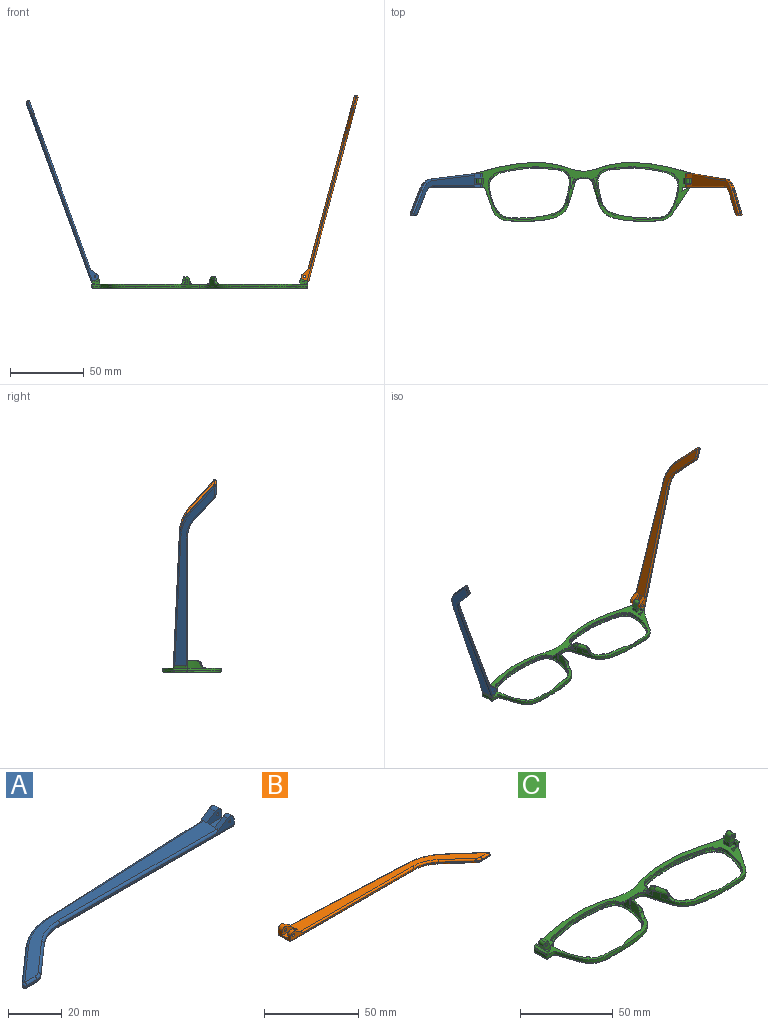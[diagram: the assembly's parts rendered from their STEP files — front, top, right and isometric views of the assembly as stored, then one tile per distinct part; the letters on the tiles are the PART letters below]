
ASSEMBLY  parts=3 mates=2
PART A: 43 faces, bbox 130.2x29.5x5.9 mm
  f0: plane 9.62x3.72mm, normal (1,0,0), area 24.7mm2, adj f1,f3,f4,f5,f10,f16,f18,f28
  f1: cylinder r=2.2mm len=3.45mm, axis (0,-1,0), area 11mm2, adj f0,f2,f4,f37
  f2: plane 6.01x3.91mm, normal (-0.55,0,0.84), area 12.7mm2, adj f1,f4,f9,f19,f37
  f3: plane 2.26x0.1mm, normal (0,0,1), area 0.1mm2, adj f0,f5,f18
  f4: plane 92.1x4.9mm, normal (0,-1,0), area 79.9mm2, adj f0,f1,f2,f14,f19,f36,f42
  f5: plane 93.42x4.13mm, normal (-0.04,1,0), area 64.8mm2, adj f0,f3,f11,f15,f17,f27,f28
  f6: plane 17.82x15.72mm, normal (-0.66,0.75,0), area 14.3mm2, adj f11,f12,f25,f30
  f7: plane 5.46x0.6mm, normal (0,-1,0), area 3.3mm2, adj f12,f13,f23,f32
  f8: plane 14.99x13.23mm, normal (0.66,-0.75,0), area 12mm2, adj f13,f14,f21,f34
  f9: plane 121.18x26.73mm, normal (0,0,1), area 627.7mm2, adj f2,f17,f19,f20,f21,f22,f23,f25
  f10: plane 129.1x27.08mm, normal (0,0,-1), area 686.5mm2, adj f0,f28,f29,f30,f32,f33,f34,f35
  f11: cylinder r=30mm len=18.52mm, axis (0,0,-1), area 12.2mm2, adj f5,f6,f26,f29
  f12: cylinder r=1mm len=1.75mm, axis (0,0,-1), area 1.5mm2, adj f6,f7,f24,f31
  f13: cylinder r=5mm len=3.31mm, axis (0,0,-1), area 2.2mm2, adj f7,f8,f22,f33
  f14: cylinder r=20mm len=13.23mm, axis (0,0,1), area 8.7mm2, adj f4,f8,f20,f35
  f15: plane 5.66x0.25mm, normal (0,0,-1), area 0.7mm2, adj f5,f17,f18
  f16: cylinder r=2.2mm len=3.45mm, axis (0,-1,0), area 14.8mm2, adj f0,f17,f18,f38
  f17: plane 6.01x3.91mm, normal (-0.55,0,0.84), area 16.9mm2, adj f5,f9,f15,f16,f18,f27,f38
  f18: plane 7.92x3.3mm, normal (0,1,0), area 15.9mm2, adj f0,f3,f15,f16,f17,f41
  f19: cylinder r=1mm len=84.18mm, axis (-1,0,0), area 131.4mm2, adj f2,f4,f9,f20
  f20: torus R=21mm, axis (0,0,1), area 23.1mm2, adj f9,f14,f19,f21
  f21: cylinder r=1mm len=15.65mm, axis (-0.75,-0.66,0), area 31.4mm2, adj f8,f9,f20,f22
  f22: torus R=4mm, axis (0,0,1), area 5.3mm2, adj f9,f13,f21,f23
  f23: cylinder r=1mm len=5.46mm, axis (-1,0,0), area 8.6mm2, adj f7,f9,f22,f24
  f24: sphere r=1mm, area 2.4mm2, adj f12,f23,f25
  f25: cylinder r=1mm len=18.48mm, axis (0.75,0.66,0), area 37.3mm2, adj f6,f9,f24,f26
  f26: torus R=29mm, axis (0,0,1), area 31.6mm2, adj f9,f11,f25,f27
  f27: cylinder r=1mm len=85.5mm, axis (1,0.04,0), area 133.5mm2, adj f5,f9,f17,f26
  f28: cylinder r=1mm len=93.46mm, axis (-1,-0.04,0), area 146.9mm2, adj f0,f5,f10,f29
  f29: torus R=29mm, axis (0,0,1), area 31.6mm2, adj f10,f11,f28,f30
  f30: cylinder r=1mm len=18.48mm, axis (-0.75,-0.66,0), area 37.3mm2, adj f6,f10,f29,f31
  f31: sphere r=1mm, area 2.4mm2, adj f12,f30,f32
  f32: cylinder r=1mm len=5.46mm, axis (1,0,0), area 8.6mm2, adj f7,f10,f31,f33
  f33: torus R=4mm, axis (0,0,1), area 5.3mm2, adj f10,f13,f32,f34
  f34: cylinder r=1mm len=15.65mm, axis (0.75,0.66,0), area 31.4mm2, adj f8,f10,f33,f35
  f35: torus R=21mm, axis (0,0,1), area 23.1mm2, adj f10,f14,f34,f36
  f36: cylinder r=1mm len=92.1mm, axis (1,0,0), area 144.7mm2, adj f0,f4,f10,f35
  f37: plane 7.92x4.7mm, normal (0,1,0), area 27mm2, adj f0,f1,f2,f39,f40,f42
  f38: plane 7.92x4.7mm, normal (0,-1,0), area 27mm2, adj f0,f16,f17,f39,f40,f41
  f39: plane 7.92x4.1mm, normal (0,0,1), area 32.5mm2, adj f0,f37,f38,f40
  f40: plane 4.1x1.4mm, normal (1,0,0), area 5.7mm2, adj f9,f37,f38,f39
  f41: cylinder r=0.5mm len=3.1mm, axis (0,-1,0), area 9.7mm2, adj f18,f38
  f42: cylinder r=0.5mm len=2.3mm, axis (0,-1,0), area 7.2mm2, adj f4,f37
PART B: 43 faces, bbox 130.2x29.5x5.9 mm
  f0: plane 9.62x3.72mm, normal (-1,0,0), area 24.7mm2, adj f1,f3,f4,f5,f10,f16,f18,f28
  f1: cylinder r=2.2mm len=3.45mm, axis (0,-1,0), area 11mm2, adj f0,f2,f4,f37
  f2: plane 6.01x3.91mm, normal (0.55,0,0.84), area 12.7mm2, adj f1,f4,f9,f19,f37
  f3: plane 2.26x0.1mm, normal (0,0,1), area 0.1mm2, adj f0,f5,f18
  f4: plane 92.1x4.9mm, normal (0,-1,0), area 78.2mm2, adj f0,f1,f2,f14,f19,f36,f42
  f5: plane 93.42x4.13mm, normal (0.04,1,0), area 64.8mm2, adj f0,f3,f11,f15,f17,f27,f28
  f6: plane 17.82x15.72mm, normal (0.66,0.75,0), area 14.3mm2, adj f11,f12,f25,f30
  f7: plane 5.46x0.6mm, normal (0,-1,0), area 3.3mm2, adj f12,f13,f23,f32
  f8: plane 14.99x13.23mm, normal (-0.66,-0.75,0), area 12mm2, adj f13,f14,f21,f34
  f9: plane 121.18x26.73mm, normal (0,0,1), area 627.7mm2, adj f2,f17,f19,f20,f21,f22,f23,f25
  f10: plane 129.1x27.08mm, normal (0,0,-1), area 686.5mm2, adj f0,f28,f29,f30,f32,f33,f34,f35
  f11: cylinder r=30mm len=18.52mm, axis (0,0,-1), area 12.2mm2, adj f5,f6,f26,f29
  f12: cylinder r=1mm len=1.75mm, axis (0,0,-1), area 1.5mm2, adj f6,f7,f24,f31
  f13: cylinder r=5mm len=3.31mm, axis (0,0,-1), area 2.2mm2, adj f7,f8,f22,f33
  f14: cylinder r=20mm len=13.23mm, axis (0,0,1), area 8.7mm2, adj f4,f8,f20,f35
  f15: plane 5.66x0.25mm, normal (0,0,-1), area 0.7mm2, adj f5,f17,f18
  f16: cylinder r=2.2mm len=3.45mm, axis (0,-1,0), area 14.8mm2, adj f0,f17,f18,f38
  f17: plane 6.01x3.91mm, normal (0.55,0,0.84), area 16.9mm2, adj f5,f9,f15,f16,f18,f27,f38
  f18: plane 7.92x3.3mm, normal (0,1,0), area 14.3mm2, adj f0,f3,f15,f16,f17,f41
  f19: cylinder r=1mm len=84.18mm, axis (1,0,0), area 131.4mm2, adj f2,f4,f9,f20
  f20: torus R=21mm, axis (0,0,1), area 23.1mm2, adj f9,f14,f19,f21
  f21: cylinder r=1mm len=15.65mm, axis (0.75,-0.66,0), area 31.4mm2, adj f8,f9,f20,f22
  f22: torus R=4mm, axis (0,0,1), area 5.3mm2, adj f9,f13,f21,f23
  f23: cylinder r=1mm len=5.46mm, axis (1,0,0), area 8.6mm2, adj f7,f9,f22,f24
  f24: sphere r=1mm, area 2.4mm2, adj f12,f23,f25
  f25: cylinder r=1mm len=18.48mm, axis (-0.75,0.66,0), area 37.3mm2, adj f6,f9,f24,f26
  f26: torus R=29mm, axis (0,0,1), area 31.6mm2, adj f9,f11,f25,f27
  f27: cylinder r=1mm len=85.5mm, axis (-1,0.04,0), area 133.5mm2, adj f5,f9,f17,f26
  f28: cylinder r=1mm len=93.46mm, axis (1,-0.04,0), area 146.9mm2, adj f0,f5,f10,f29
  f29: torus R=29mm, axis (0,0,1), area 31.6mm2, adj f10,f11,f28,f30
  f30: cylinder r=1mm len=18.48mm, axis (0.75,-0.66,0), area 37.3mm2, adj f6,f10,f29,f31
  f31: sphere r=1mm, area 2.4mm2, adj f12,f30,f32
  f32: cylinder r=1mm len=5.46mm, axis (-1,0,0), area 8.6mm2, adj f7,f10,f31,f33
  f33: torus R=4mm, axis (0,0,1), area 5.3mm2, adj f10,f13,f32,f34
  f34: cylinder r=1mm len=15.65mm, axis (-0.75,0.66,0), area 31.4mm2, adj f8,f10,f33,f35
  f35: torus R=21mm, axis (0,0,1), area 23.1mm2, adj f10,f14,f34,f36
  f36: cylinder r=1mm len=92.1mm, axis (-1,0,0), area 144.7mm2, adj f0,f4,f10,f35
  f37: plane 7.92x4.7mm, normal (0,1,0), area 25.4mm2, adj f0,f1,f2,f39,f40,f42
  f38: plane 7.92x4.7mm, normal (0,-1,0), area 25.4mm2, adj f0,f16,f17,f39,f40,f41
  f39: plane 7.92x4.1mm, normal (0,0,1), area 32.5mm2, adj f0,f37,f38,f40
  f40: plane 4.1x1.4mm, normal (-1,0,0), area 5.7mm2, adj f9,f37,f38,f39
  f41: cylinder r=0.88mm len=3.1mm, axis (0,-1,0), area 17mm2, adj f18,f38
  f42: cylinder r=0.88mm len=2.3mm, axis (0,-1,0), area 12.6mm2, adj f4,f37
PART C: 120 faces, bbox 148.1x40.9x17.9 mm
  f0: bspline ~1.82x1.22mm, area 0.7mm2, adj f2,f7,f38,f53
  f1: plane 147.57x40.34mm, normal (0,0,1), area 849mm2, adj f4,f5,f6,f7,f8,f9,f13,f21
  f2: bspline ~6.1x4.93mm, area 12.7mm2, adj f0,f7,f38,f42,f44,f53,f54
  f3: plane 4.46x1.45mm, normal (0,0,1), area 0.1mm2, adj f7,f39
  f4: plane 1.23x0.04mm, normal (0,0,1), area 0mm2, adj f1,f7,f23
  f5: plane 6.97x5.07mm, normal (0,1,0), area 22.7mm2, adj f1,f21,f22,f26,f28,f29,f31,f32
  f6: plane 3.2x2.36mm, normal (0,-1,0), area 5.7mm2, adj f1,f21,f27,f30
  f7: extruded ~73.26x39.84mm, area 292.7mm2, adj f0,f1,f2,f3,f4,f8,f14,f15
  f8: extruded ~35.39x5.69mm, area 72.2mm2, adj f1,f7,f19,f68
  f9: extruded ~9.91x2mm, area 20.1mm2, adj f1,f12,f13,f20
  f10: plane 144.78x37.85mm, normal (0,0,-1), area 582.4mm2, adj f14,f16,f18,f19,f20,f73,f75,f77
  f11: plane 56.11x36.01mm, normal (0,0,1), area 126.3mm2, adj f12,f20
  f12: extruded ~55.66x35.79mm, area 147mm2, adj f9,f11,f13
  f13: extruded ~55.66x35.79mm, area 197.8mm2, adj f1,f9,f12,f40,f41,f42,f43,f44
  f14: bspline ~73.27x30.39mm, area 161.7mm2, adj f7,f10,f15,f73
  f15: bspline ~1x1mm, area 0.8mm2, adj f7,f14,f16
  f16: bspline ~8.99x1.23mm, area 12.6mm2, adj f7,f10,f15,f17
  f17: bspline ~1.04x1mm, area 0.7mm2, adj f7,f16,f18
  f18: bspline ~45.86x8.59mm, area 59.8mm2, adj f7,f10,f17,f19
  f19: bspline ~37.01x6.7mm, area 56.6mm2, adj f8,f10,f18,f78
  f20: bspline ~56.23x35.9mm, area 235.3mm2, adj f9,f10,f11
  f21: plane 4x2.36mm, normal (-1,0,0), area 9.5mm2, adj f1,f5,f6,f22
  f22: plane 4x0.02mm, normal (0.34,0,0.94), area 0.1mm2, adj f5,f21,f29
  f23: plane 2.76x2.53mm, normal (0,-1,0), area 3.9mm2, adj f4,f27,f28,f36,f57
  f24: plane 7.67x1.6mm, normal (0.94,0,-0.34), area 13mm2, adj f1,f36,f37,f57
  f25: plane 2.1x1.69mm, normal (0,1,0), area 2.8mm2, adj f1,f26,f28,f37,f57
  f26: plane 3.3x2.1mm, normal (-1,0,0), area 6.9mm2, adj f1,f5,f25,f28
  f27: plane 2.35x2.1mm, normal (-1,0,0), area 4.9mm2, adj f1,f6,f23,f28,f30
  f28: plane 9.65x1.24mm, normal (0,0,1), area 8.2mm2, adj f5,f23,f25,f26,f27,f30,f31,f57
  f29: plane 4x3.31mm, normal (-0.94,0,0.34), area 14.1mm2, adj f5,f22,f30,f33
  f30: plane 5.77x5.06mm, normal (0,-1,0), area 17mm2, adj f6,f27,f28,f29,f31,f32,f33,f34
  f31: plane 4x2.21mm, normal (0.94,0,-0.34), area 9.4mm2, adj f5,f28,f30,f34
  f32: plane 4x0.01mm, normal (0.34,0,0.94), area 0mm2, adj f5,f30,f33,f34
  f33: cylinder r=1.98mm len=4mm, axis (0,1,0), area 12.4mm2, adj f5,f29,f30,f32
  f34: cylinder r=1.98mm len=4mm, axis (0,-1,0), area 12.4mm2, adj f5,f30,f31,f32
  f35: cylinder r=0.88mm len=4mm, axis (0,-1,0), area 22mm2, adj f5,f30
  f36: cone r=1mm half-angle=20deg, axis (0,0,1), area 2.3mm2, adj f1,f23,f24,f57
  f37: cylinder r=1mm len=2.28mm, axis (-0.34,0,-0.94), area 3mm2, adj f1,f24,f25,f57
  f38: extruded ~3.67x3.11mm, area 5.9mm2, adj f0,f2,f7,f60
  f39: extruded ~4.44x3.32mm, area 15.1mm2, adj f3,f7,f43,f44,f56
  f40: extruded ~4.98x1.36mm, area 6.6mm2, adj f13,f42
  f41: plane 3.63x0.97mm, normal (0,0,1), area 0.3mm2, adj f13,f42,f44
  f42: bspline ~15.5x15.35mm, area 6.4mm2, adj f2,f13,f40,f41,f55
  f43: bspline ~7.26x7.26mm, area 6.3mm2, adj f13,f39,f44,f56
  f44: bspline ~10.29x4.84mm, area 21.4mm2, adj f2,f7,f13,f39,f41,f43
  f45: plane 3.19x1.37mm, normal (0,0,-1), area 2.1mm2, adj f13,f46
  f46: cylinder r=2.28mm len=3.17mm, axis (0,0,1), area 2.1mm2, adj f1,f13,f45,f55
  f47: plane 3.14x2.79mm, normal (0,0,-1), area 3.9mm2, adj f13,f48
  f48: cylinder r=2.28mm len=3.13mm, axis (0,0,1), area 2.5mm2, adj f1,f13,f47
  f49: plane 1.8x1.27mm, normal (0,0,-1), area 0.9mm2, adj f13,f50
  f50: cylinder r=1.3mm len=1.79mm, axis (0,0,1), area 1.3mm2, adj f1,f13,f49
  f51: plane 1.95x1.68mm, normal (0,0,-1), area 1.5mm2, adj f13,f52
  f52: cylinder r=1.3mm len=1.93mm, axis (0,0,1), area 1.5mm2, adj f1,f13,f51
  f53: bspline ~2.66x2.04mm, area 1.9mm2, adj f0,f2,f7,f54,f59
  f54: bspline ~3.55x3.47mm, area 3.7mm2, adj f1,f2,f53,f55,f59
  f55: bspline ~5.1x3.97mm, area 7.9mm2, adj f1,f13,f42,f46,f54
  f56: bspline ~3.7x3.66mm, area 7.8mm2, adj f1,f7,f13,f39,f43
  f57: plane 9.71x1.44mm, normal (0.34,0,0.94), area 13.9mm2, adj f23,f24,f25,f28,f36,f37
  f58: bspline ~6.38x2.14mm, area 2.6mm2, adj f1,f7,f59,f117
  f59: bspline ~2.1x1.46mm, area 0.6mm2, adj f7,f53,f54,f58
  f60: bspline ~5.24x1.75mm, area 0mm2, adj f7,f38
  f61: bspline ~2.19x1.4mm, area 0.7mm2, adj f62,f67,f97,f112
  f62: bspline ~6.1x4.93mm, area 12.6mm2, adj f61,f67,f97,f101,f103,f112,f113
  f63: plane 4.46x1.45mm, normal (0,0,1), area 0.1mm2, adj f67,f98
  f64: plane 1.23x0.04mm, normal (0,0,1), area 0mm2, adj f1,f67,f82
  f65: plane 6.97x5.07mm, normal (0,1,0), area 22.7mm2, adj f1,f80,f81,f85,f87,f88,f90,f91
  f66: plane 3.2x2.36mm, normal (0,-1,0), area 5.7mm2, adj f1,f80,f86,f89
  f67: extruded ~73.26x39.84mm, area 292.7mm2, adj f1,f7,f61,f62,f63,f64,f68,f73
  f68: extruded ~35.39x5.69mm, area 72.2mm2, adj f1,f8,f67,f78
  f69: extruded ~9.91x2mm, area 20.1mm2, adj f1,f71,f72,f79
  f70: plane 56.11x36.01mm, normal (0,0,1), area 126.3mm2, adj f71,f79
  f71: extruded ~55.66x35.79mm, area 147mm2, adj f69,f70,f72
  f72: extruded ~55.66x35.79mm, area 197.8mm2, adj f1,f69,f71,f99,f100,f101,f102,f103
  f73: bspline ~73.83x30.39mm, area 161.7mm2, adj f10,f14,f67,f74
  f74: bspline ~1x1mm, area 0.8mm2, adj f67,f73,f75
  f75: bspline ~8.99x1.23mm, area 12.6mm2, adj f10,f67,f74,f76
  f76: bspline ~1.04x1mm, area 0.8mm2, adj f67,f75,f77
  f77: bspline ~45.86x8.59mm, area 59.8mm2, adj f10,f67,f76,f78
  f78: bspline ~37.01x6.7mm, area 56.6mm2, adj f10,f19,f68,f77
  f79: bspline ~56.22x35.9mm, area 235.3mm2, adj f10,f69,f70
  f80: plane 4x2.36mm, normal (1,0,0), area 9.5mm2, adj f1,f65,f66,f81
  f81: plane 4x0.02mm, normal (-0.34,0,0.94), area 0.1mm2, adj f65,f80,f88
  f82: plane 2.76x2.53mm, normal (0,-1,0), area 3.9mm2, adj f64,f86,f87,f95,f116
  f83: plane 7.67x1.6mm, normal (-0.94,0,-0.34), area 13mm2, adj f1,f95,f96,f116
  f84: plane 2.1x1.69mm, normal (0,1,0), area 2.8mm2, adj f1,f85,f87,f96,f116
  f85: plane 3.3x2.1mm, normal (1,0,0), area 6.9mm2, adj f1,f65,f84,f87
  f86: plane 2.35x2.1mm, normal (1,0,0), area 4.9mm2, adj f1,f66,f82,f87,f89
  f87: plane 9.65x1.24mm, normal (0,0,1), area 8.2mm2, adj f65,f82,f84,f85,f86,f89,f90,f116
  f88: plane 4x3.31mm, normal (0.94,0,0.34), area 14.1mm2, adj f65,f81,f89,f92
  f89: plane 5.77x5.06mm, normal (0,-1,0), area 17mm2, adj f66,f86,f87,f88,f90,f91,f92,f93
  f90: plane 4x2.21mm, normal (-0.94,0,-0.34), area 9.4mm2, adj f65,f87,f89,f93
  f91: plane 4x0.01mm, normal (-0.34,0,0.94), area 0mm2, adj f65,f89,f92,f93
  f92: cylinder r=1.98mm len=4mm, axis (0,1,0), area 12.4mm2, adj f65,f88,f89,f91
  f93: cylinder r=1.98mm len=4mm, axis (0,-1,0), area 12.4mm2, adj f65,f89,f90,f91
  f94: cylinder r=0.88mm len=4mm, axis (0,-1,0), area 22mm2, adj f65,f89
  f95: cone r=1mm half-angle=20deg, axis (0,0,1), area 2.3mm2, adj f1,f82,f83,f116
  f96: cylinder r=1mm len=2.28mm, axis (0.34,0,-0.94), area 3mm2, adj f1,f83,f84,f116
  f97: extruded ~3.67x3.11mm, area 5.9mm2, adj f61,f62,f67,f119
  f98: extruded ~4.44x3.32mm, area 15.1mm2, adj f63,f67,f102,f103,f115
  f99: extruded ~4.98x1.36mm, area 6.6mm2, adj f72,f101
  f100: plane 3.63x0.97mm, normal (0,0,1), area 0.3mm2, adj f72,f101,f103
  f101: bspline ~15.5x15.35mm, area 6.4mm2, adj f62,f72,f99,f100,f114
  f102: bspline ~7.26x7.26mm, area 6.2mm2, adj f72,f98,f103,f115
  f103: bspline ~10.29x4.84mm, area 21.5mm2, adj f62,f67,f72,f98,f100,f102
  f104: plane 3.19x1.37mm, normal (0,0,-1), area 2.1mm2, adj f72,f105
  f105: cylinder r=2.28mm len=3.17mm, axis (0,0,1), area 2.1mm2, adj f1,f72,f104,f114
  f106: plane 3.14x2.79mm, normal (0,0,-1), area 3.9mm2, adj f72,f107
  f107: cylinder r=2.28mm len=3.13mm, axis (0,0,1), area 2.5mm2, adj f1,f72,f106
  f108: plane 1.8x1.27mm, normal (0,0,-1), area 0.9mm2, adj f72,f109
  f109: cylinder r=1.3mm len=1.79mm, axis (0,0,1), area 1.3mm2, adj f1,f72,f108
  f110: plane 1.95x1.68mm, normal (0,0,-1), area 1.5mm2, adj f72,f111
  f111: cylinder r=1.3mm len=1.93mm, axis (0,0,1), area 1.5mm2, adj f1,f72,f110
  f112: bspline ~2.65x2.03mm, area 1.9mm2, adj f61,f62,f67,f113,f118
  f113: bspline ~3.55x3.47mm, area 3.7mm2, adj f1,f62,f112,f114,f118
  f114: bspline ~5.94x4.42mm, area 7.9mm2, adj f1,f72,f101,f105,f113
  f115: bspline ~3.7x3.66mm, area 7.8mm2, adj f1,f67,f72,f98,f102
  f116: plane 9.71x1.44mm, normal (-0.34,0,0.94), area 13.9mm2, adj f82,f83,f84,f87,f95,f96
  f117: bspline ~6.38x2.14mm, area 2.6mm2, adj f1,f58,f67,f118
  f118: bspline ~2.1x1.46mm, area 0.6mm2, adj f67,f112,f113,f117
  f119: bspline ~5.24x1.75mm, area 0mm2, adj f67,f97
PLACE A rot(axis=(0,1,0),70deg) t=(-84.77,-5.75,56)mm
PLACE B rot(axis=(0,-1,0),75deg) t=(68.2,-5.75,-61.61)mm
PLACE C t=(10.15,-1.13,-5.77)mm
MATE revolute A.f1 <-> C.f92  axis (0,-1,0) through (-60.89,2.72,1.22)mm
MATE revolute B.f41 <-> C.f34  axis (0,-1,0) through (81.2,2.72,1.21)mm
